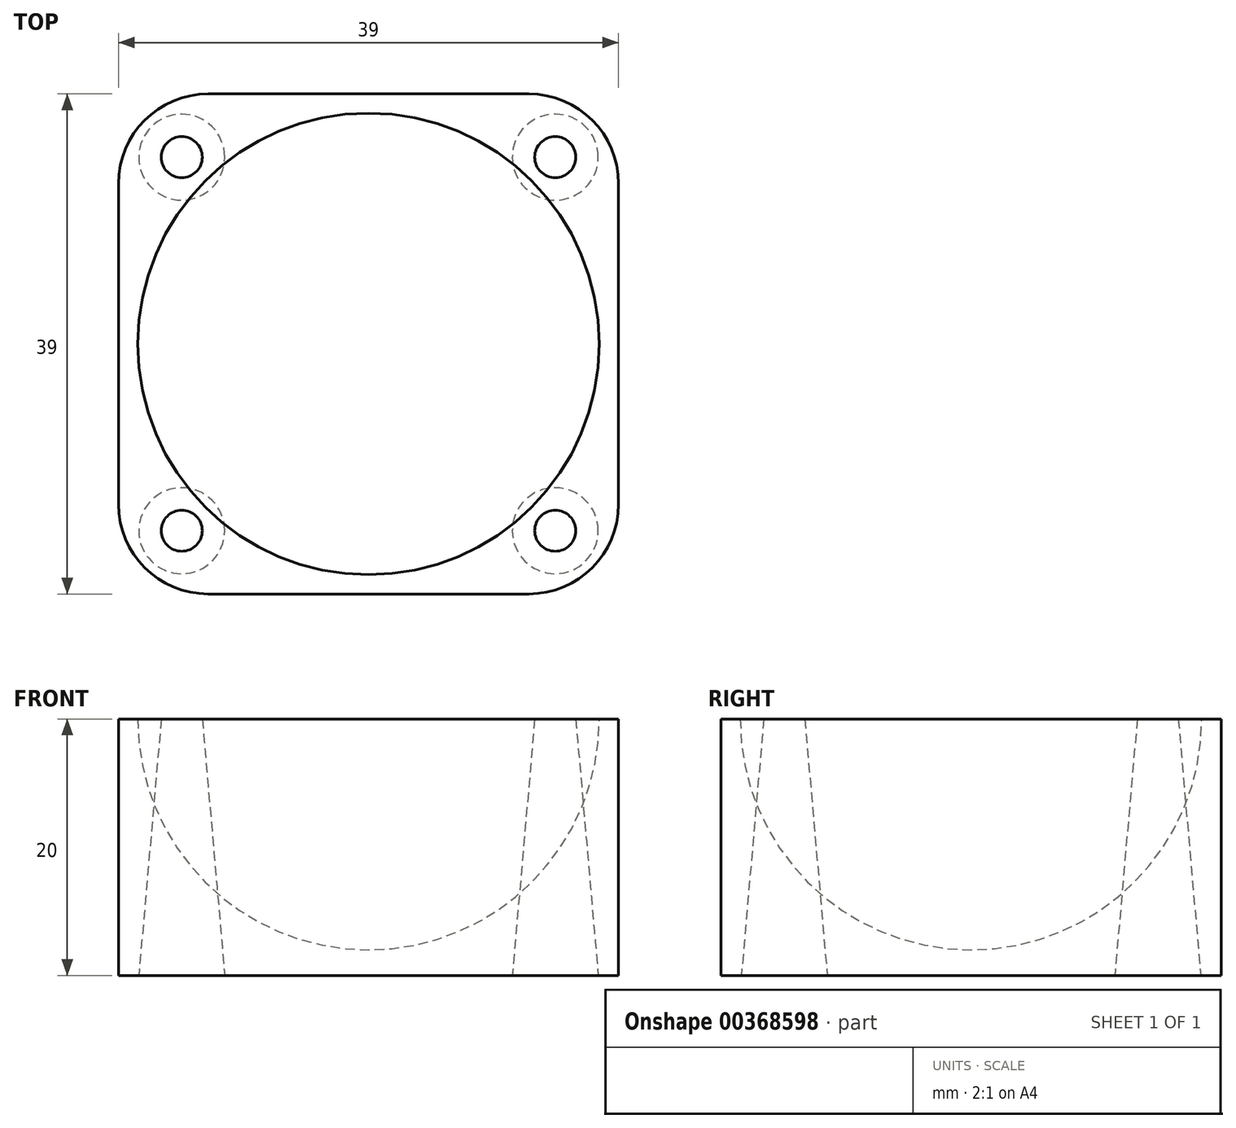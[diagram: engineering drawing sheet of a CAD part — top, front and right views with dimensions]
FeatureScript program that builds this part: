
annotation { "Feature Type Name" : "Feature", "Feature Type Description" : "" }
export const myFeature = defineFeature(function(context is Context, id is Id, definition is map)
    precondition{}
    {
        {
            var Q0;
            Q0=qCreatedBy(makeId("Top.planeOp"),FACE);
            var sketch = newSketch(context, id + "F0", { "sketchPlane" : qUnion([Q0])});
            skArc(sketch, "E0", {"start": v(36, 0) * mm, "mid": v(18, 18) * mm, "end": v(0, 0) * mm});
            skLineSegment(sketch, "E1", {"start": v(0, 0) * mm, "end": v(36, 0) * mm});
            skLineSegment(sketch, "E2.bottom", {"start": v(37.5, 19.5) * mm, "end": v(-1.5, 19.5) * mm});
            skLineSegment(sketch, "E2.top", {"start": v(37.5, -19.5) * mm, "end": v(-1.5, -19.5) * mm});
            skLineSegment(sketch, "E2.left", {"start": v(37.5, 19.5) * mm, "end": v(37.5, -19.5) * mm});
            skLineSegment(sketch, "E2.right", {"start": v(-1.5, 19.5) * mm, "end": v(-1.5, -19.5) * mm});
            skSolve(sketch);
        }
        {
            var Q0;
            Q0=makeQuery(id+"F0.imprint","IMPRINT",FACE,{"disambiguationData":[TD([[makeQuery(id+"F0.imprint","IMPRINT",EDGE,{"derivedFrom":sQuery(id+"F0.wireOp",EDGE,"E0")}),1.0]])]});
            var Q1;
            Q1=sQuery(id+"F0.wireOp",EDGE,"E1");
            revolve(context, id + "F1", {"entities" : qUnion([Q0]), "axis" : qUnion([Q1]), "revolveType" : RevolveType.FULL});
        }
        {
            var Q0;
            Q0=qCreatedBy(makeId("Top.planeOp"),FACE);
            var sketch = newSketch(context, id + "F2", { "sketchPlane" : qUnion([Q0])});
            skLineSegment(sketch, "E3.0", {"start": v(37.5, 19.5) * mm, "end": v(-1.5, 19.5) * mm});
            skLineSegment(sketch, "E3.1", {"start": v(37.5, 19.5) * mm, "end": v(37.5, -19.5) * mm});
            skLineSegment(sketch, "E3.2", {"start": v(37.5, -19.5) * mm, "end": v(-1.5, -19.5) * mm});
            skLineSegment(sketch, "E3.3", {"start": v(-1.5, 19.5) * mm, "end": v(-1.5, -19.5) * mm});
            skSolve(sketch);
        }
        {
            var Q0;
            Q0 = qSketchRegion(id + "F2", true);
            extrude(context, id + "F3", {"entities" : qUnion([Q0]), "oppositeDirection" : true, "depth" : 20 * mm});
        }
        {
            var Q0;
            Q0=makeQuery(id+"F1.opRevolve","SWEPT_BODY",BODY,{"disambiguationData":[OSD([sQuery(id+"F0.wireOp",EDGE,"E0"),sQuery(id+"F0.wireOp",EDGE,"E1")])]});
            var Q1;
            Q1=makeQuery(id+"F3.opExtrude","SWEPT_BODY",BODY,{"disambiguationData":[OSD([sQuery(id+"F2.wireOp",EDGE,"E3.0"),sQuery(id+"F2.wireOp",EDGE,"E3.1"),sQuery(id+"F2.wireOp",EDGE,"E3.2"),sQuery(id+"F2.wireOp",EDGE,"E3.3")])]});
            booleanBodies(context, id + "F4", {"operationType" : BooleanOperationType.SUBTRACTION, "tools" : qUnion([Q0]), "targets" : qUnion([Q1])});
        }
        {
            var Q0;
            Q0=makeQuery(id+"F3.opExtrude","SWEPT_EDGE",EDGE,{"disambiguationData":[OSD([sQuery(id+"F2.wireOp",EDGE,"E3.2"),sQuery(id+"F2.wireOp",EDGE,"E3.3")])]});
            var Q1;
            Q1=makeQuery(id+"F3.opExtrude","SWEPT_EDGE",EDGE,{"disambiguationData":[OSD([sQuery(id+"F2.wireOp",EDGE,"E3.1"),sQuery(id+"F2.wireOp",EDGE,"E3.2")])]});
            var Q2;
            Q2=makeQuery(id+"F3.opExtrude","SWEPT_EDGE",EDGE,{"disambiguationData":[OSD([sQuery(id+"F2.wireOp",EDGE,"E3.0"),sQuery(id+"F2.wireOp",EDGE,"E3.1")])]});
            var Q3;
            Q3=makeQuery(id+"F3.opExtrude","SWEPT_EDGE",EDGE,{"disambiguationData":[OSD([sQuery(id+"F2.wireOp",EDGE,"E3.0"),sQuery(id+"F2.wireOp",EDGE,"E3.3")])]});
            fillet(context, id + "F5", {"entities" : qUnion([Q0, Q1, Q2, Q3]), "radius" : 7 * mm, "tangentPropagation" : true, "allowEdgeOverflow" : false});
        }
        {
            var Q0;
            Q0=makeQuery(id+"F3.opExtrude","CAP_FACE",FACE,{"disambiguationData":[OSD([sQuery(id+"F2.wireOp",EDGE,"E3.0"),sQuery(id+"F2.wireOp",EDGE,"E3.1"),sQuery(id+"F2.wireOp",EDGE,"E3.2"),sQuery(id+"F2.wireOp",EDGE,"E3.3")])],"isStart":true});
            var sketch = newSketch(context, id + "F6", { "sketchPlane" : qUnion([Q0])});
            skCircle(sketch, "E4.0", {"center": v(18, 0) * mm, "radius": 18 * mm});
            skLineSegment(sketch, "E5", {"start": v(18, 0) * mm, "end": v(35.45, 17.45) * mm, "construction": true});
            skLineSegment(sketch, "E6", {"start": v(35.45, 17.45) * mm, "end": v(30.73, 12.73) * mm, "construction": true});
            skCircle(sketch, "E7", {"center": v(32.57, 14.57) * mm, "radius": 1.6 * mm});
            skCircle(sketch, "E8.1.0", {"center": v(3.43, 14.57) * mm, "radius": 1.6 * mm});
            skCircle(sketch, "E8.2.0", {"center": v(3.43, -14.57) * mm, "radius": 1.6 * mm});
            skCircle(sketch, "E8.3.0", {"center": v(32.57, -14.57) * mm, "radius": 1.6 * mm});
            skSolve(sketch);
        }
        {
            var Q0;
            Q0=makeQuery(id+"F6.imprint","IMPRINT",FACE,{"disambiguationData":[TD([[makeQuery(id+"F6.imprint","IMPRINT",EDGE,{"derivedFrom":sQuery(id+"F6.wireOp",EDGE,"E7")}),1.0]])]});
            var Q1;
            Q1=makeQuery(id+"F6.imprint","IMPRINT",FACE,{"disambiguationData":[TD([[makeQuery(id+"F6.imprint","IMPRINT",EDGE,{"derivedFrom":sQuery(id+"F6.wireOp",EDGE,"E8.1.0")}),1.0]])]});
            var Q2;
            Q2=makeQuery(id+"F6.imprint","IMPRINT",FACE,{"disambiguationData":[TD([[makeQuery(id+"F6.imprint","IMPRINT",EDGE,{"derivedFrom":sQuery(id+"F6.wireOp",EDGE,"E8.2.0")}),1.0]])]});
            var Q3;
            Q3=makeQuery(id+"F6.imprint","IMPRINT",FACE,{"disambiguationData":[TD([[makeQuery(id+"F6.imprint","IMPRINT",EDGE,{"derivedFrom":sQuery(id+"F6.wireOp",EDGE,"E8.3.0")}),1.0]])]});
            extrude(context, id + "F7", {"entities" : qUnion([Q0, Q1, Q2, Q3]), "operationType" : NewBodyOperationType.REMOVE, "endBound" : BoundingType.THROUGH_ALL, "oppositeDirection" : true, "depth" : 25 * mm, "hasDraft" : true, "draftAngle" : 5 * degree});
        }
    });
